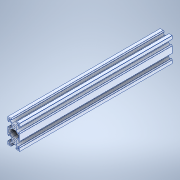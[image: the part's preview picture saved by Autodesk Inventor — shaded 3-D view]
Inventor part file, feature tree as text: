
AUTODESK INVENTOR PART (.ipt)
format: ipt  version: 2020 (Build 240168000, 168)  size: 219,136 bytes
history: mixed  units: in
note: dims shown in document units (in); Inventor stores cm internally (conversion verified against a paired STEP export)
features: mirror x1, imported_body x1
ambient origin geometry x8: Origin, YZ Plane, XZ Plane, XY Plane, X Axis, Y Axis, Z Axis, Center Point
bodies: Solid1 (imported_parasolid)
feature tree (2):
  mirror  "Mirror2"
  imported_body  NMx_Import_Brep_tag  [imported B-rep: ~128 faces, bbox_mm=[20.0, 40.0, 250.0]]
